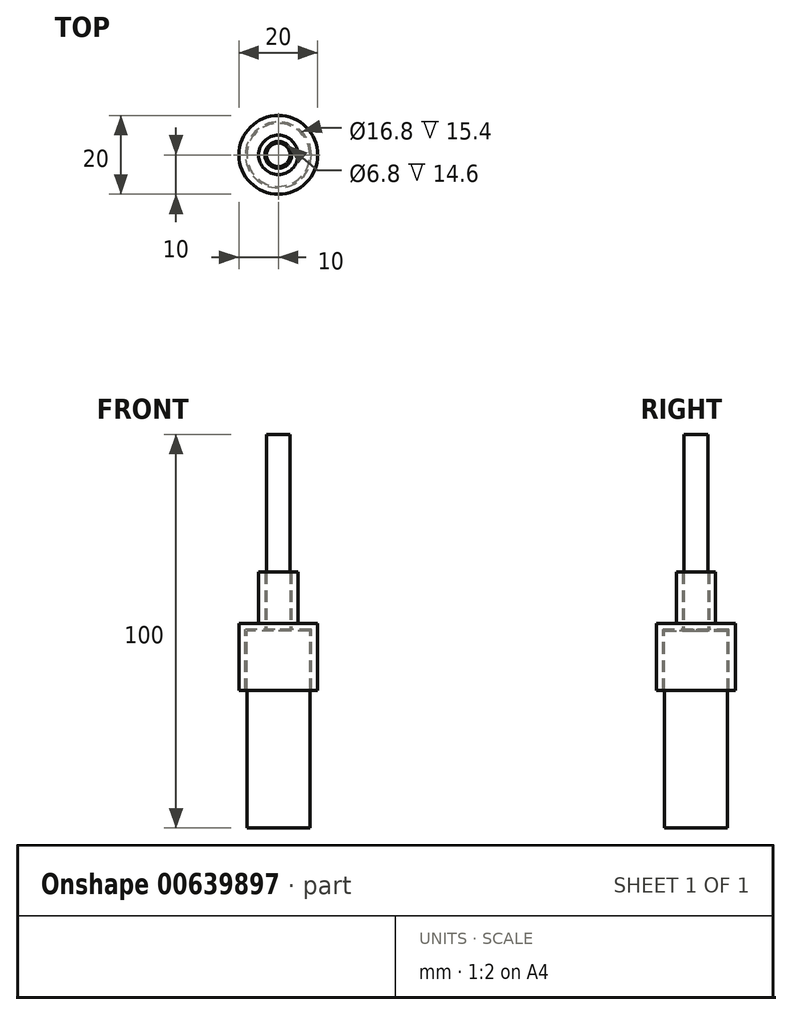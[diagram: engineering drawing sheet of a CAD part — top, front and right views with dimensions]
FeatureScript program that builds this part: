
annotation { "Feature Type Name" : "Feature", "Feature Type Description" : "" }
export const myFeature = defineFeature(function(context is Context, id is Id, definition is map)
    precondition{}
    {
        {
            var Q0;
            Q0=qCreatedBy(makeId("Top.planeOp"),FACE);
            var sketch = newSketch(context, id + "F0", { "sketchPlane" : qUnion([Q0])});
            skCircle(sketch, "E0", {"center": v(0, 0) * mm, "radius": 3 * mm});
            skCircle(sketch, "E1", {"center": v(0, 0) * mm, "radius": 8 * mm});
            skLineSegment(sketch, "E2", {"start": v(0, 0) * mm, "end": v(0, -62.51) * mm, "construction": true});
            skSolve(sketch);
        }
        {
            var Q0;
            Q0=makeQuery(id+"F0.imprint","IMPRINT",FACE,{"disambiguationData":[TD([[makeQuery(id+"F0.imprint","IMPRINT",EDGE,{"derivedFrom":sQuery(id+"F0.wireOp",EDGE,"E0")}),1.0]])]});
            extrude(context, id + "F1", {"entities" : qUnion([Q0]), "depth" : 50 * mm, "offsetDistance" : 25 * mm});
        }
        {
            var Q0;
            Q0=makeQuery(id+"F0.imprint","IMPRINT",FACE,{"disambiguationData":[TD([[makeQuery(id+"F0.imprint","IMPRINT",EDGE,{"derivedFrom":sQuery(id+"F0.wireOp",EDGE,"E0")}),1.0]])]});
            var Q1;
            Q1=makeQuery(id+"F0.imprint","IMPRINT",FACE,{"disambiguationData":[TD([[makeQuery(id+"F0.imprint","IMPRINT",EDGE,{"derivedFrom":sQuery(id+"F0.wireOp",EDGE,"E0")}),-1.0]])]});
            extrude(context, id + "F2", {"entities" : qUnion([Q0, Q1]), "operationType" : NewBodyOperationType.ADD, "oppositeDirection" : true, "depth" : 50 * mm, "offsetDistance" : 25 * mm});
        }
        {
            var Q0;
            Q0=makeQuery(id+"F2.opExtrude","CAP_FACE",FACE,{"disambiguationData":[OSD([sQuery(id+"F0.wireOp",EDGE,"E1")])],"isStart":true});
            var sketch = newSketch(context, id + "F3", { "sketchPlane" : qUnion([Q0])});
            skCircle(sketch, "E3", {"center": v(0, 0) * mm, "radius": 10 * mm});
            skSolve(sketch);
        }
        {
            var Q0;
            Q0 = qSketchRegion(id + "F3", true);
            extrude(context, id + "F4", {"entities" : qUnion([Q0]), "endBound" : BoundingType.SYMMETRIC, "depth" : 30 * mm, "offsetDistance" : 25 * mm});
        }
        {
            var Q0;
            Q0=makeQuery(id+"F1.opExtrude","SWEPT_BODY",BODY,{"disambiguationData":[OSD([sQuery(id+"F0.wireOp",EDGE,"E0")])]});
            var Q1;
            Q1=makeQuery(id+"F4.opExtrude","SWEPT_BODY",BODY,{"disambiguationData":[OSD([sQuery(id+"F3.wireOp",EDGE,"E3")])]});
            booleanBodies(context, id + "F5", {"operationType" : BooleanOperationType.SUBTRACTION, "tools" : qUnion([Q0]), "targets" : qUnion([Q1]), "offset" : true, "offsetAll" : true, "offsetDistance" : .4 * mm, "keepTools" : true});
        }
        {
            var Q0;
            Q0=makeQuery(id+"F4.opExtrude","CAP_FACE",FACE,{"disambiguationData":[OSD([sQuery(id+"F3.wireOp",EDGE,"E3")])],"isStart":false});
            var Q1;
            Q1=makeQuery(id+"F4.opExtrude","SWEPT_FACE",FACE,{"disambiguationData":[OSD([sQuery(id+"F3.wireOp",EDGE,"E3")])]});
            shell(context, id + "F6", {"entities" : qUnion([Q0, Q1]), "thickness" : 1.6 * mm});
        }
    });
